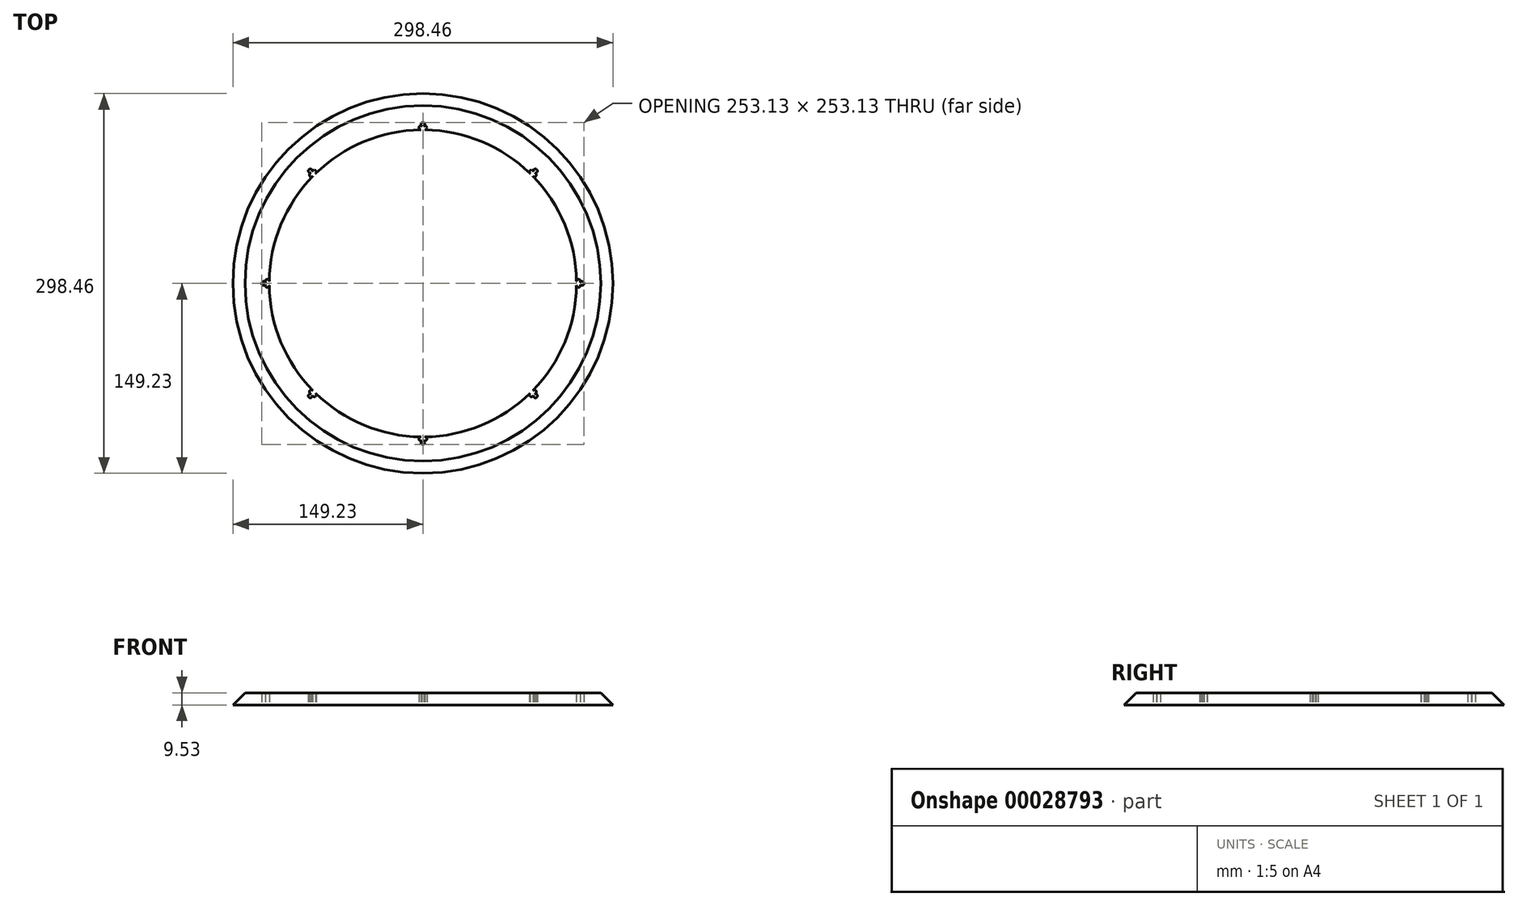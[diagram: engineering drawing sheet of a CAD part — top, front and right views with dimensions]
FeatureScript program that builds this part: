
annotation { "Feature Type Name" : "Feature", "Feature Type Description" : "" }
export const myFeature = defineFeature(function(context is Context, id is Id, definition is map)
    precondition{}
    {
        {
            var Q0;
            Q0=qCreatedBy(makeId("Top.planeOp"),FACE);
            var sketch = newSketch(context, id + "F0", { "sketchPlane" : qUnion([Q0])});
            skCircle(sketch, "E0", {"center": v(0, 0) * mm, "radius": 149.23 * mm});
            skCircle(sketch, "E1", {"center": v(0, 0) * mm, "radius": 120.65 * mm});
            skLineSegment(sketch, "E2", {"start": v(-149.23, 0) * mm, "end": v(149.23, 0) * mm});
            skLineSegment(sketch, "E3", {"start": v(0, 0) * mm, "end": v(0, -149.23) * mm});
            skLineSegment(sketch, "E4", {"start": v(0, 0) * mm, "end": v(0, 149.23) * mm});
            skLineSegment(sketch, "E5", {"start": v(0, 0) * mm, "end": v(-149.23, 0) * mm});
            skLineSegment(sketch, "E6.top", {"start": v(-149.23, -149.23) * mm, "end": v(149.23, -149.23) * mm});
            skLineSegment(sketch, "E6.left", {"start": v(-149.23, 0) * mm, "end": v(-149.23, -149.23) * mm});
            skLineSegment(sketch, "E6.right", {"start": v(149.23, 0) * mm, "end": v(149.23, -149.23) * mm});
            skLineSegment(sketch, "E7.top", {"start": v(-149.23, 149.23) * mm, "end": v(149.23, 149.23) * mm});
            skLineSegment(sketch, "E7.left", {"start": v(-149.23, 0) * mm, "end": v(-149.23, 149.23) * mm});
            skLineSegment(sketch, "E7.right", {"start": v(149.23, 0) * mm, "end": v(149.23, 149.23) * mm});
            skLineSegment(sketch, "E8", {"start": v(-149.23, 149.23) * mm, "end": v(149.23, -149.23) * mm});
            skLineSegment(sketch, "E9", {"start": v(149.23, 149.23) * mm, "end": v(-149.23, -149.23) * mm});
            skCircle(sketch, "E10", {"center": v(-1.59, 122.23) * mm, "radius": 1.59 * mm});
            skCircle(sketch, "E11", {"center": v(1.59, 122.23) * mm, "radius": 1.59 * mm});
            skCircle(sketch, "E12", {"center": v(0, 124.98) * mm, "radius": 1.59 * mm});
            skCircle(sketch, "E13", {"center": v(88.37, 88.37) * mm, "radius": 1.59 * mm});
            skCircle(sketch, "E14", {"center": v(87.55, 85.3) * mm, "radius": 1.59 * mm});
            skCircle(sketch, "E15", {"center": v(85.3, 87.55) * mm, "radius": 1.59 * mm});
            skCircle(sketch, "E16", {"center": v(124.98, 0) * mm, "radius": 1.59 * mm});
            skCircle(sketch, "E17", {"center": v(122.23, 1.59) * mm, "radius": 1.59 * mm});
            skCircle(sketch, "E18", {"center": v(122.23, -1.59) * mm, "radius": 1.59 * mm});
            skCircle(sketch, "E19", {"center": v(88.37, -88.37) * mm, "radius": 1.59 * mm});
            skCircle(sketch, "E20", {"center": v(87.55, -85.3) * mm, "radius": 1.59 * mm});
            skCircle(sketch, "E21", {"center": v(85.3, -87.55) * mm, "radius": 1.59 * mm});
            skCircle(sketch, "E22", {"center": v(0, -124.98) * mm, "radius": 1.59 * mm});
            skCircle(sketch, "E23", {"center": v(1.59, -122.23) * mm, "radius": 1.59 * mm});
            skCircle(sketch, "E24", {"center": v(-1.59, -122.23) * mm, "radius": 1.59 * mm});
            skCircle(sketch, "E25", {"center": v(-88.37, -88.37) * mm, "radius": 1.59 * mm});
            skCircle(sketch, "E26", {"center": v(-87.55, -85.3) * mm, "radius": 1.59 * mm});
            skCircle(sketch, "E27", {"center": v(-85.3, -87.55) * mm, "radius": 1.59 * mm});
            skCircle(sketch, "E28", {"center": v(-124.98, 0) * mm, "radius": 1.59 * mm});
            skCircle(sketch, "E29", {"center": v(-122.23, 1.59) * mm, "radius": 1.59 * mm});
            skCircle(sketch, "E30", {"center": v(-122.23, -1.59) * mm, "radius": 1.59 * mm});
            skCircle(sketch, "E31", {"center": v(-88.37, 88.37) * mm, "radius": 1.59 * mm});
            skCircle(sketch, "E32", {"center": v(-85.3, 87.55) * mm, "radius": 1.59 * mm});
            skCircle(sketch, "E33", {"center": v(-87.55, 85.3) * mm, "radius": 1.59 * mm});
            skSolve(sketch);
        }
        {
            var Q0;
            {var subQ0=sQuery(id+"F0.wireOp",EDGE,"E33");var subQ3=sQuery(id+"F0.wireOp",EDGE,"E1");var subQ4=makeQuery(id+"F0.imprint","INTERSECT",VERTEX,{"derivedFrom":[subQ3,subQ0]});Q0=makeQuery(id+"F0.imprint","IMPRINT",FACE,{"disambiguationData":[TD([[makeQuery(id+"F0.imprint","IMPRINT",EDGE,{"disambiguationData":[TD([[subQ4,-1.0]])],"derivedFrom":subQ3}),-1.0]])]});}
            var Q1;
            {var subQ0=sQuery(id+"F0.wireOp",EDGE,"E30");var subQ3=sQuery(id+"F0.wireOp",EDGE,"E1");var subQ4=makeQuery(id+"F0.imprint","INTERSECT",VERTEX,{"derivedFrom":[subQ3,subQ0]});Q1=makeQuery(id+"F0.imprint","IMPRINT",FACE,{"disambiguationData":[TD([[makeQuery(id+"F0.imprint","IMPRINT",EDGE,{"disambiguationData":[TD([[subQ4,-1.0]])],"derivedFrom":subQ3}),-1.0]])]});}
            var Q2;
            {var subQ1=sQuery(id+"F0.wireOp",EDGE,"E27");var subQ10=sQuery(id+"F0.wireOp",EDGE,"E1");var subQ14=makeQuery(id+"F0.imprint","INTERSECT",VERTEX,{"derivedFrom":[subQ10,subQ1]});Q2=makeQuery(id+"F0.imprint","IMPRINT",FACE,{"disambiguationData":[TD([[makeQuery(id+"F0.imprint","IMPRINT",EDGE,{"disambiguationData":[TD([[subQ14,-1.0]])],"derivedFrom":subQ10}),-1.0]])]});}
            var Q3;
            {var subQ0=sQuery(id+"F0.wireOp",EDGE,"E23");var subQ3=sQuery(id+"F0.wireOp",EDGE,"E1");var subQ4=makeQuery(id+"F0.imprint","INTERSECT",VERTEX,{"derivedFrom":[subQ3,subQ0]});Q3=makeQuery(id+"F0.imprint","IMPRINT",FACE,{"disambiguationData":[TD([[makeQuery(id+"F0.imprint","IMPRINT",EDGE,{"disambiguationData":[TD([[subQ4,-1.0]])],"derivedFrom":subQ3}),-1.0]])]});}
            var Q4;
            {var subQ0=sQuery(id+"F0.wireOp",EDGE,"E20");var subQ3=sQuery(id+"F0.wireOp",EDGE,"E1");var subQ4=makeQuery(id+"F0.imprint","INTERSECT",VERTEX,{"derivedFrom":[subQ3,subQ0]});Q4=makeQuery(id+"F0.imprint","IMPRINT",FACE,{"disambiguationData":[TD([[makeQuery(id+"F0.imprint","IMPRINT",EDGE,{"disambiguationData":[TD([[subQ4,-1.0]])],"derivedFrom":subQ3}),-1.0]])]});}
            var Q5;
            {var subQ0=sQuery(id+"F0.wireOp",EDGE,"E17");var subQ3=sQuery(id+"F0.wireOp",EDGE,"E1");var subQ4=makeQuery(id+"F0.imprint","INTERSECT",VERTEX,{"derivedFrom":[subQ3,subQ0]});Q5=makeQuery(id+"F0.imprint","IMPRINT",FACE,{"disambiguationData":[TD([[makeQuery(id+"F0.imprint","IMPRINT",EDGE,{"disambiguationData":[TD([[subQ4,-1.0]])],"derivedFrom":subQ3}),-1.0]])]});}
            var Q6;
            {var subQ1=sQuery(id+"F0.wireOp",EDGE,"E15");var subQ10=sQuery(id+"F0.wireOp",EDGE,"E1");var subQ15=makeQuery(id+"F0.imprint","INTERSECT",VERTEX,{"derivedFrom":[subQ10,subQ1]});Q6=makeQuery(id+"F0.imprint","IMPRINT",FACE,{"disambiguationData":[TD([[makeQuery(id+"F0.imprint","IMPRINT",EDGE,{"disambiguationData":[TD([[subQ15,-1.0]])],"derivedFrom":subQ10}),-1.0]])]});}
            var Q7;
            {var subQ3=sQuery(id+"F0.wireOp",EDGE,"E1");var subQ8=sQuery(id+"F0.wireOp",EDGE,"E10");var subQ12=makeQuery(id+"F0.imprint","INTERSECT",VERTEX,{"derivedFrom":[subQ3,subQ8]});Q7=makeQuery(id+"F0.imprint","IMPRINT",FACE,{"disambiguationData":[TD([[makeQuery(id+"F0.imprint","IMPRINT",EDGE,{"disambiguationData":[TD([[subQ12,-1.0]])],"derivedFrom":subQ3}),-1.0]])]});}
            extrude(context, id + "F1", {"entities" : qUnion([Q0, Q1, Q2, Q3, Q4, Q5, Q6, Q7]), "depth" : 9.52 * mm});
        }
        {
            var Q0;
            Q0=makeQuery(id+"F1.opExtrude","CAP_EDGE",EDGE,{"disambiguationData":[OSD([sQuery(id+"F0.wireOp",EDGE,"E0")])],"isStart":false});
            chamfer(context, id + "F2", {"entities" : qUnion([Q0]), "width" : 9.52 * mm, "tangentPropagation" : true});
        }
    });
